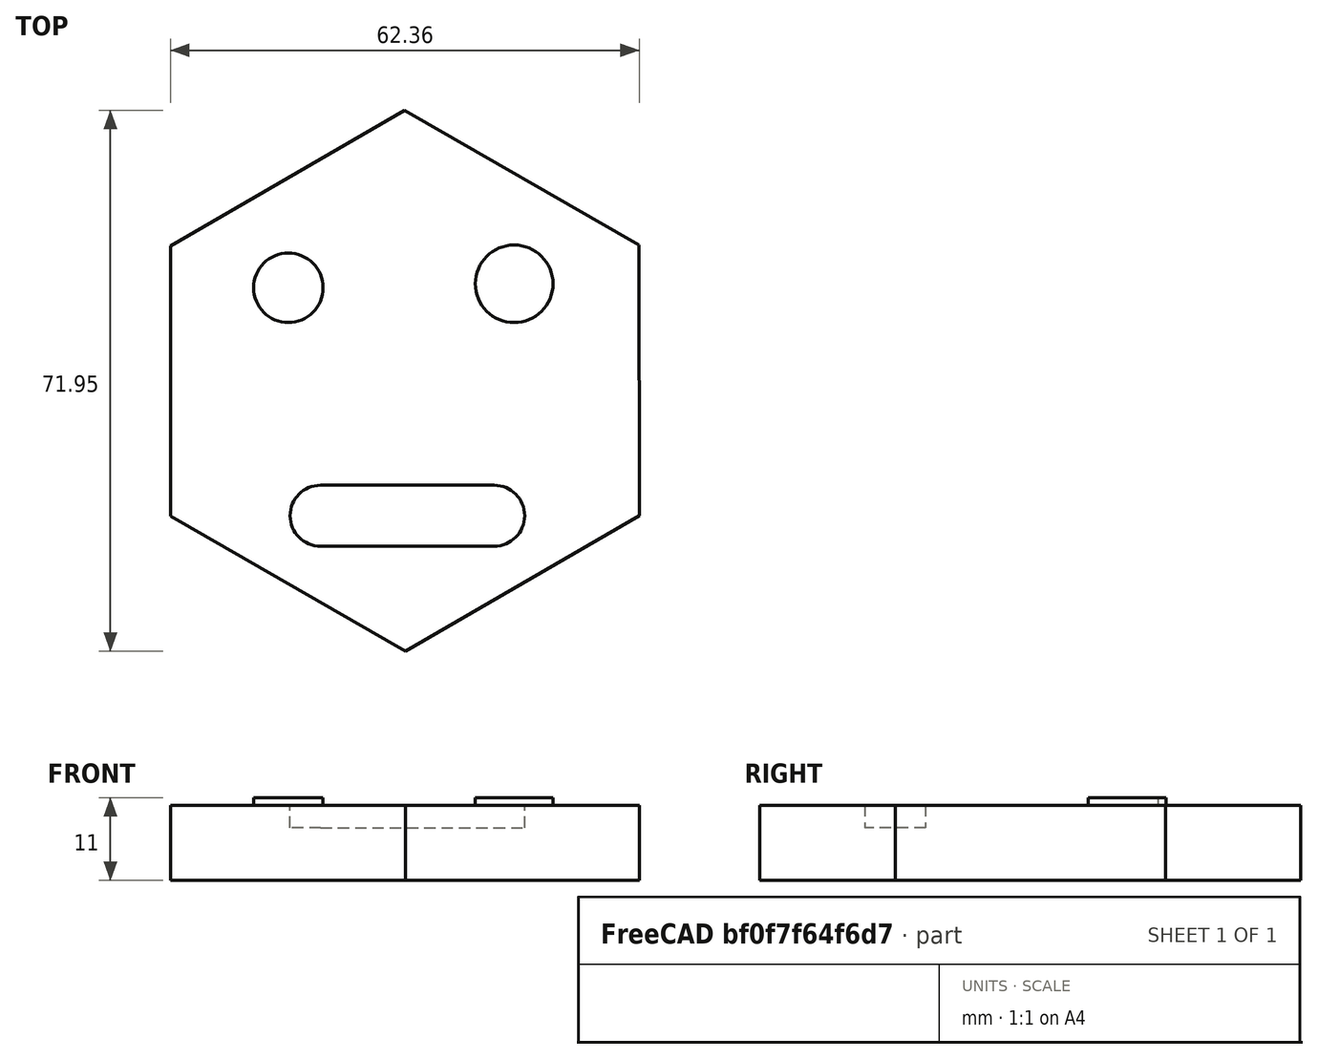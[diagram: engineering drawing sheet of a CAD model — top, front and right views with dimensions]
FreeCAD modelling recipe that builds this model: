
FCSTD DOCUMENT  (FreeCAD 1.0R38642 (Git))
Label: Opgave_1.1.4
License: All rights reserved
LicenseURL: http://en.wikipedia.org/wiki/All_rights_reserved
objects: PartDesign::Pad×2, Sketcher::SketchObject×1, PartDesign::Pocket×1, PartDesign::Body×1
note: 12 computed .brp shape members not serialized (recipe doc carries the construction recipe); baked Part::Feature solids carry a one-line shape summary decoded from their .brp

FEATURE [Sketcher::SketchObject] Sketch
  ArcFitTolerance = 1e-06
  AttachmentSupport = -> [XY_Plane]
  FullyConstrained = false
  MakeInternals = false
  MapMode = 5
  sketch-geometry (17):
    g0: LineSegment StartX=96.7236 StartY=31.1383 StartZ=0 EndX=96.6741 EndY=67.1161 EndZ=0
    g1: LineSegment StartX=96.6741 StartY=67.1161 StartZ=0 EndX=65.4917 EndY=85.0621 EndZ=0
    g2: LineSegment StartX=65.4917 StartY=85.0621 StartZ=0 EndX=34.3588 EndY=67.0304 EndZ=0
    g3: LineSegment StartX=34.3588 StartY=67.0304 StartZ=0 EndX=34.4083 EndY=31.0527 EndZ=0
    g4: LineSegment StartX=34.4083 StartY=31.0527 StartZ=0 EndX=65.5907 EndY=13.1066 EndZ=0
    g5: LineSegment StartX=65.5907 StartY=13.1066 StartZ=0 EndX=96.7236 EndY=31.1383 EndZ=0
    g6: Circle [constr] CenterX=65.5412 CenterY=49.0844 CenterZ=0 NormalX=0 NormalY=0 NormalZ=1 AngleXU=0 Radius=35.9778
    g7: Circle CenterX=50.0453 CenterY=61.4527 CenterZ=0 NormalX=0 NormalY=0 NormalZ=1 AngleXU=0 Radius=4.61885
    g8: Circle CenterX=80.0827 CenterY=61.986 CenterZ=0 NormalX=0 NormalY=0 NormalZ=1 AngleXU=0 Radius=5.15796
    g9: ArcOfCircle CenterX=54.3254 CenterY=31.1269 CenterZ=0 NormalX=0 NormalY=0 NormalZ=1 AngleXU=0 Radius=4.05549 StartAngle=1.5708 EndAngle=4.71239
    g10: ArcOfCircle CenterX=77.4117 CenterY=31.1269 CenterZ=0 NormalX=0 NormalY=0 NormalZ=1 AngleXU=0 Radius=4.05549 StartAngle=4.71239 EndAngle=7.85398
    g11: LineSegment StartX=54.3254 StartY=35.1823 StartZ=0 EndX=77.4117 EndY=35.1823 EndZ=0
    g12: LineSegment StartX=54.3254 StartY=27.0714 StartZ=0 EndX=77.4117 EndY=27.0714 EndZ=0
    g13: LineSegment StartX=65.5538 StartY=55.2965 StartZ=0 EndX=60.155 EndY=45.9892 EndZ=0
    g14: LineSegment StartX=60.155 StartY=45.9892 StartZ=0 EndX=70.9148 EndY=45.9674 EndZ=0
    g15: LineSegment StartX=70.9148 StartY=45.9674 StartZ=0 EndX=65.5538 EndY=55.2965 EndZ=0
    g16: Circle [constr] CenterX=65.5412 CenterY=49.0844 CenterZ=0 NormalX=0 NormalY=0 NormalZ=1 AngleXU=0 Radius=6.21217
  constraints (28):
    c: Coincident(g0,g1)
    c: Coincident(g1,g2)
    c: Coincident(g2,g3)
    c: Coincident(g3,g4)
    c: Coincident(g4,g5)
    c: Coincident(g5,g0)
    c: Equal(g0, g1-g5) x5
    c: PointOnObject(g0,g6)
    c: PointOnObject(g1,g6)
    c: PointOnObject(g2,g6)
    c: PointOnObject(g3,g6)
    c: PointOnObject(g4,g6)
    c: PointOnObject(g5,g6)
    c: Tangent(g9,g11) = 1.5708
    c: Tangent(g9,g12) = -1.5708
    c: Tangent(g10,g11) = 1.5708
    c: Tangent(g10,g12) = -1.5708
    c: Equal(g9,g10)
    c: Horizontal(g12)
    c: Coincident(g13,g14)
    c: Coincident(g14,g15)
    c: Coincident(g15,g13)
    c: Equal(g13,g14)
    c: Equal(g13,g15)
    c: PointOnObject(g13,g16)
    c: PointOnObject(g14,g16)
    c: PointOnObject(g15,g16)
    c: Coincident(g6,g16)
FEATURE [PartDesign::Pad] Pad
  Direction = (0,0,1)
  Length = 10
  Length2 = 10
  Profile = -> Sketch [Edge4,Edge3,Edge2,Edge1,Edge6,Edge5]
  ReferenceAxis = -> Sketch [N_Axis]
  Refine = true
  Reversed = true
  Suppressed = false
  Type = 0
FEATURE [PartDesign::Pocket] Pocket
  BaseFeature = -> Pad
  Direction = (0,0,-1)
  Length = 3
  Length2 = 5
  Profile = -> Sketch [Edge10,Edge12,Edge9,Edge11]
  ReferenceAxis = -> Sketch [N_Axis]
  Refine = true
  Suppressed = false
  Type = 0
FEATURE [PartDesign::Pad] Pad001
  BaseFeature = -> Pocket
  Direction = (0,0,1)
  Length = 1
  Length2 = 10
  Profile = -> Sketch [Edge7,Edge8]
  ReferenceAxis = -> Sketch [N_Axis]
  Refine = true
  Suppressed = false
  Type = 0
FEATURE [PartDesign::Body] Body
  AllowCompound = true
  Group = -> [Sketch,Pad,Pocket,Pad001]
  Origin = -> Origin
  Tip = -> Pad001
